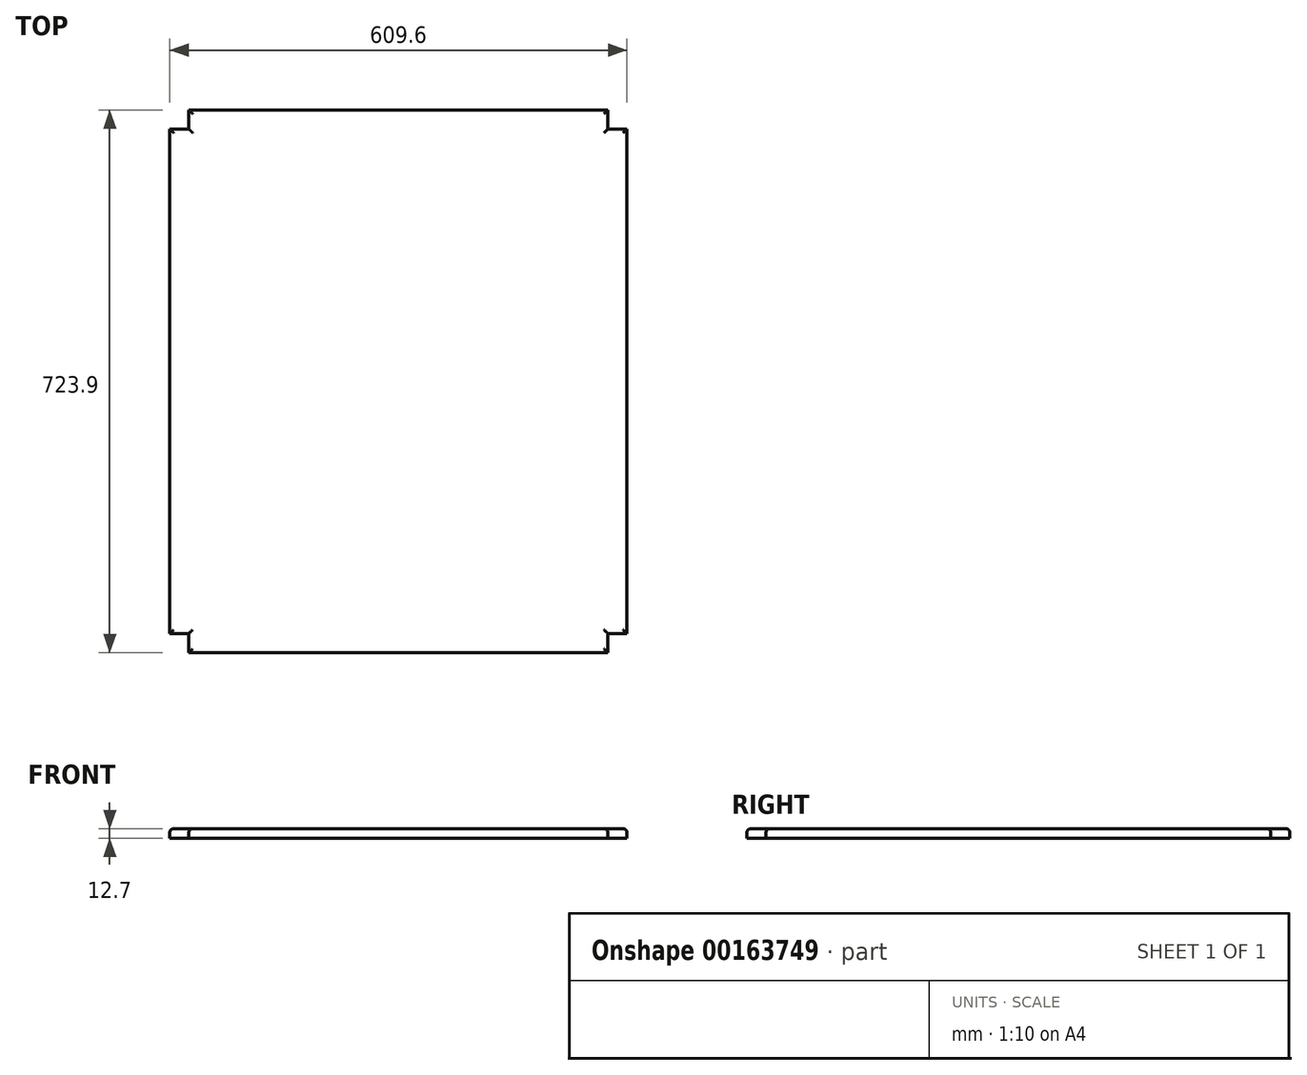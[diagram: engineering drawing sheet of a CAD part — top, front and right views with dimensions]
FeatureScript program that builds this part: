
annotation { "Feature Type Name" : "Feature", "Feature Type Description" : "" }
export const myFeature = defineFeature(function(context is Context, id is Id, definition is map)
    precondition{}
    {
        {
            var Q0;
            Q0=qCreatedBy(makeId("Top.planeOp"),FACE);
            var sketch = newSketch(context, id + "F0", { "sketchPlane" : qUnion([Q0])});
            skLineSegment(sketch, "E0.bottom", {"start": v(-279.4, 361.95) * mm, "end": v(279.4, 361.95) * mm});
            skLineSegment(sketch, "E0.top", {"start": v(-279.4, -361.95) * mm, "end": v(279.4, -361.95) * mm});
            skLineSegment(sketch, "E0.left", {"start": v(-304.8, 336.55) * mm, "end": v(-304.8, -336.55) * mm});
            skLineSegment(sketch, "E0.right", {"start": v(304.8, 336.55) * mm, "end": v(304.8, -336.55) * mm});
            skPoint(sketch, "E0.middle", {"position": v(0, 0) * mm});
            skPoint(sketch, "E1.visualSharp", {"position": v(-304.8, 361.95) * mm});
            skPoint(sketch, "E2.visualSharp", {"position": v(304.8, 361.95) * mm});
            skPoint(sketch, "E3.visualSharp", {"position": v(304.8, -361.95) * mm});
            skPoint(sketch, "E4.visualSharp", {"position": v(-304.8, -361.95) * mm});
            skLineSegment(sketch, "E5.top", {"start": v(-304.8, -336.55) * mm, "end": v(-279.4, -336.55) * mm});
            skLineSegment(sketch, "E5.right", {"start": v(-279.4, -361.95) * mm, "end": v(-279.4, -336.55) * mm});
            skLineSegment(sketch, "E6.top", {"start": v(-304.8, 336.55) * mm, "end": v(-279.4, 336.55) * mm});
            skLineSegment(sketch, "E6.right", {"start": v(-279.4, 361.95) * mm, "end": v(-279.4, 336.55) * mm});
            skLineSegment(sketch, "E7.top", {"start": v(304.8, 336.55) * mm, "end": v(279.4, 336.55) * mm});
            skLineSegment(sketch, "E7.right", {"start": v(279.4, 361.95) * mm, "end": v(279.4, 336.55) * mm});
            skLineSegment(sketch, "E8.top", {"start": v(304.8, -336.55) * mm, "end": v(279.4, -336.55) * mm});
            skLineSegment(sketch, "E8.right", {"start": v(279.4, -361.95) * mm, "end": v(279.4, -336.55) * mm});
            skSolve(sketch);
        }
        {
            var Q0;
            Q0=qSketchRegion(id+"F0",true);
            extrude(context, id + "F1", {"entities" : qUnion([Q0]), "depth" : 12.7 * mm});
        }
        {
            var Q0;
            Q0=makeQuery(id+"F1.opExtrude","CAP_EDGE",EDGE,{"disambiguationData":[OSD([sQuery(id+"F0.wireOp",EDGE,"E0.left")])],"isStart":false});
            var Q1;
            Q1=makeQuery(id+"F1.opExtrude","CAP_EDGE",EDGE,{"disambiguationData":[OSD([sQuery(id+"F0.wireOp",EDGE,"E0.top")])],"isStart":false});
            var Q2;
            Q2=makeQuery(id+"F1.opExtrude","CAP_EDGE",EDGE,{"disambiguationData":[OSD([sQuery(id+"F0.wireOp",EDGE,"E0.right")])],"isStart":false});
            var Q3;
            Q3=makeQuery(id+"F1.opExtrude","CAP_EDGE",EDGE,{"disambiguationData":[OSD([sQuery(id+"F0.wireOp",EDGE,"E0.bottom")])],"isStart":false});
            var Q4;
            Q4=makeQuery(id+"F1.opExtrude","CAP_EDGE",EDGE,{"disambiguationData":[OSD([sQuery(id+"F0.wireOp",EDGE,"E6.top")])],"isStart":false});
            var Q5;
            Q5=makeQuery(id+"F1.opExtrude","CAP_EDGE",EDGE,{"disambiguationData":[OSD([sQuery(id+"F0.wireOp",EDGE,"E6.right")])],"isStart":false});
            var Q6;
            Q6=makeQuery(id+"F1.opExtrude","CAP_EDGE",EDGE,{"disambiguationData":[OSD([sQuery(id+"F0.wireOp",EDGE,"E7.right")])],"isStart":false});
            var Q7;
            Q7=makeQuery(id+"F1.opExtrude","CAP_EDGE",EDGE,{"disambiguationData":[OSD([sQuery(id+"F0.wireOp",EDGE,"E7.top")])],"isStart":false});
            var Q8;
            Q8=makeQuery(id+"F1.opExtrude","CAP_EDGE",EDGE,{"disambiguationData":[OSD([sQuery(id+"F0.wireOp",EDGE,"E5.top")])],"isStart":false});
            var Q9;
            Q9=makeQuery(id+"F1.opExtrude","CAP_EDGE",EDGE,{"disambiguationData":[OSD([sQuery(id+"F0.wireOp",EDGE,"E5.right")])],"isStart":false});
            var Q10;
            Q10=makeQuery(id+"F1.opExtrude","CAP_EDGE",EDGE,{"disambiguationData":[OSD([sQuery(id+"F0.wireOp",EDGE,"E8.right")])],"isStart":false});
            var Q11;
            Q11=makeQuery(id+"F1.opExtrude","CAP_EDGE",EDGE,{"disambiguationData":[OSD([sQuery(id+"F0.wireOp",EDGE,"E8.top")])],"isStart":false});
            fillet(context, id + "F2", {"entities" : qUnion([Q0, Q1, Q2, Q3, Q4, Q5, Q6, Q7, Q8, Q9, Q10, Q11]), "radius" : 5.08 * mm, "tangentPropagation" : true, "allowEdgeOverflow" : false});
        }
    });
